# Revit family: 2093108 Sylvania Lighting Fixture MC2-KIT D I 2-4M 3K DALIEM WHT OPAL
name_source: partatom
category: Lighting Fixtures
revit_build: Autodesk Revit 2016 (Build: 20150220_1215(x64)
units: mm (PartAtom-declared; Revit-internal decimal feet)

## family parameters
Cut with Voids When Loaded = No
Host = Face
Light Source = Yes
OmniClass Number = 23.80.70.11.17
OmniClass Title = Specialized Lighting by Location or Use
Part Type = Normal
Room Calculation Point = No
Round Connector Dimension = Use Diameter
Shared = No

## types (2) — shared parameters
Apparent Load = 67 VA
Assembly Code = D5020200
AssetType = Fixed
Color Filter = 16777215
Description = 2093108   MC2-KIT D/I 2.4M 3K DALIEM WHT OPAL  Continuous lines of LED light, white RAL 9016, direct/indirect distribution (65/35), suspended kit version is pre-wired and supplied complete with end caps and suspension cables, compact and minimalist design based on the Golden Mean, ideal for offices, meeting rooms, corridors, education facilities, museums and libraries, extruded aluminium body, diffuser: opal, colour temperature: 3000K warm white, total system power: 67W, total fixture output: 7666lm, luminaire efficacy: 114lm/W, LOR: 100%, colour rendering: Ra >80, LED Chromacity: 1 step MacAdam ellipse, lifetime: 60,000 hours at 90% of the original output (L90), energy class: A++, A+, A, IR/UV free light source without heat radiation, operating voltage: 220-240V / 50-60Hz, drive current: (Direct) 800mA + (Indirect) 350mA, electronic driver, DALI dimmable, direct/indirect independently addressable, integral emergency: 3 hour maintained, electrical protection: CLASS I, IP20, suitable for internal environment only.
Dimming Lamp Color Temperature Shift = <None>
DocumentationLiterature = http://www.sylvania-lighting.com
DurationUnit = hours
ElectricShockClassification = Class I
Emit Shape Visible in Rendering = No
Emit from Rectangle Length = 2400 mm
Emit from Rectangle Width = 52 mm  [stored 0.170604 ft]
EndCapLeft_SYL = Yes
EndCapRight_SYL = Yes
ExpectedLife = 50000
Height_SYL = 86 mm  [stored 0.282152 ft]
IfcExportAs = IfcLightFixtureType
IfcExportType = IfcLightFixtureType
IngressProtection = IP20
Keynote = 16500
Lamp = LED
LampColourRenderingIndex = 80
LampColourTemperature = 3000 K
LampMacAdamStep = 3
LampsType = LED
Length_SYL = 2400 mm
LightOutputRatio = 100
Manufacturer = Feilo Sylvania
ManufacturerName = Feilo Sylvania
Material = aluminium housing, polycarbonate diffuser
Material_1_SYL = Metal_Sylvania_Mini Continuum II_White
Material_2_SYL = Polycarbonate_Sylvania_Mini Continuum II_Opal_4000K
Material_3_SYL = Metal_Sylvania_Mini Contiuum II_Silver
Material_4_SYL = Metal_Sylvania_Mini Contiuum II_Silver
Model = MC2-KIT D/I 2.4M 3K DALIEM WHT OPAL
ModelNumber = 2093108
ModelReference = MC2-KIT D/I 2.4M 3K DALIEM WHT OPAL
NominalHeight = 86 mm  [stored 0.282152 ft]
NominalLength = 2400 mm
PowerConsumption = 67 W
PowerFactor = 0.95
Tilt Angle = -90.00°
URL = http://www.sylvania-lighting.com
Voltage = 0 V
Weight = 6.6 kg
Width_SYL = 54 mm  [stored 0.177165 ft]
zero-valued in all types: Default Elevation, NominalWidth

## per-type parameters (varying)
| type | LampNominalLuminous | LuminousEfficacy | Name | Photometric Web File | TypeName |
| 2093108 MC2-KIT D/I 2.4M 3K DALIEM WHT OPAL Emergency mode | 121 lm | 1.805 lm/W | MC2-KIT D/I 2.4M 3K DALIEM WHT OPAL Emergency mode | 2093108EM.ies | MC2-KIT D/I 2.4M 3K DALIEM WHT OPAL Emergency mode |
| 2093108 MC2-KIT D/I 2.4M 3K DALIEM WHT OPAL | 7666 lm | 114 lm/W | MC2-KIT D/I 2.4M 3K DALIEM WHT OPAL | 2093108.ies | MC2-KIT D/I 2.4M 3K DALIEM WHT OPAL |

note: [stored X ft] marks values corroborated as IEEE doubles in the binary element streams (Revit-internal decimal feet)

## geometry (parser evidence)
native form markers: Sweep x3
no freeform markers — native parametric forms only
